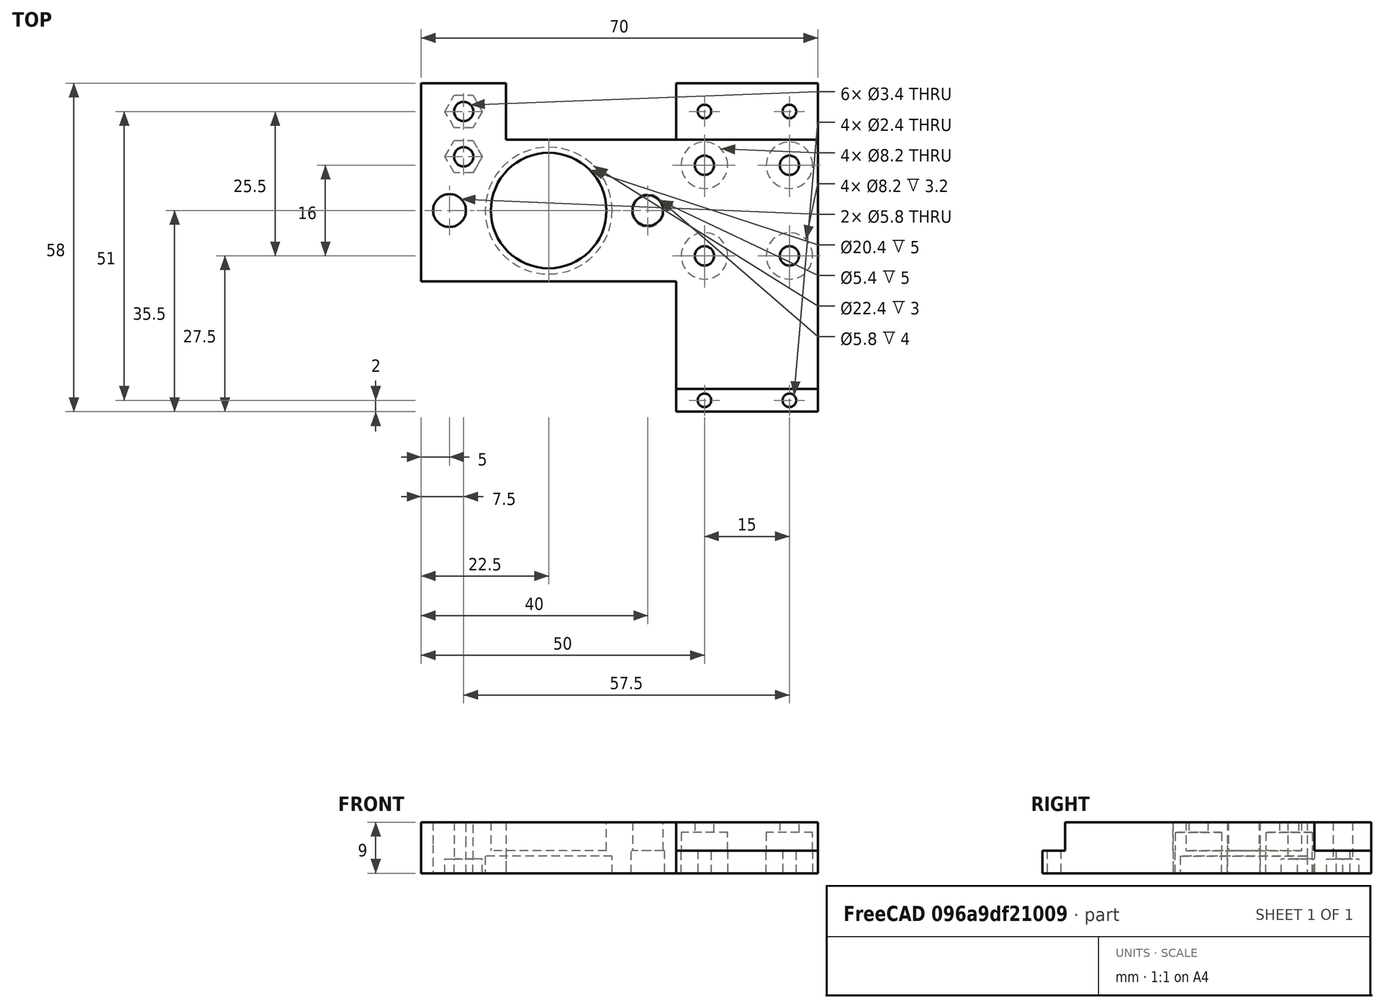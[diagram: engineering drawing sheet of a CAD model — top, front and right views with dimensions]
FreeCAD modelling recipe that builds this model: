
FCSTD DOCUMENT  (FreeCAD 0.18.4R)
Label: down_left_magnet_arm
License: All rights reserved
LicenseURL: http://en.wikipedia.org/wiki/All_rights_reserved
objects: Sketcher::SketchObject×13, PartDesign::Pocket×7, PartDesign::Pad×6, Mesh::Feature×1, PartDesign::Body×1
note: 40 computed .brp shape members not serialized (recipe doc carries the construction recipe); baked Part::Feature solids carry a one-line shape summary decoded from their .brp

FEATURE [Sketcher::SketchObject] Sketch
  MapMode = 5
  Support = -> [XY_Plane]
  sketch-geometry (10):
    g0: LineSegment StartX=-30 StartY=12.5 StartZ=0 EndX=30 EndY=12.5 EndZ=0
    g1: LineSegment StartX=30 StartY=12.5 StartZ=0 EndX=30 EndY=-12.5 EndZ=0
    g2: LineSegment StartX=30 StartY=-12.5 StartZ=0 EndX=-30 EndY=-12.5 EndZ=0
    g3: LineSegment StartX=-30 StartY=-12.5 StartZ=0 EndX=-30 EndY=12.5 EndZ=0
    g4: Circle CenterX=10 CenterY=8 CenterZ=0 NormalX=0 NormalY=0 NormalZ=1 AngleXU=0 Radius=1.7
    g5: Circle CenterX=25 CenterY=8 CenterZ=0 NormalX=0 NormalY=0 NormalZ=1 AngleXU=0 Radius=1.7
    g6: Circle CenterX=10 CenterY=-8 CenterZ=0 NormalX=0 NormalY=0 NormalZ=1 AngleXU=0 Radius=1.7
    g7: Circle CenterX=25 CenterY=-8 CenterZ=0 NormalX=0 NormalY=0 NormalZ=1 AngleXU=0 Radius=1.7
    g8: Circle CenterX=-17.5 CenterY=0 CenterZ=0 NormalX=0 NormalY=0 NormalZ=1 AngleXU=0 Radius=10.2
    g9: Circle CenterX=9e-16 CenterY=0 CenterZ=0 NormalX=0 NormalY=0 NormalZ=1 AngleXU=0 Radius=2.7
  constraints (26):
    c: Coincident(g0,g1)
    c: Coincident(g1,g2)
    c: Coincident(g2,g3)
    c: Coincident(g3,g0)
    c: Horizontal(g2)
    c: Vertical(g1)
    c: Symmetric(g0,g0,g-2)
    c: Symmetric(g0,g2,g-1)
    c: DistanceX(g0,g0) = 60
    c: DistanceY(g3,g3) = 25
    c: Symmetric(g7,g5,g-1)
    c: Symmetric(g4,g6,g-1)
    c: Distance(g6,g7) = 15
    c: Distance(g4,g6) = 16
    c: Horizontal(g5,g4)
    c: Radius(g4) = 1.7
    c: Radius(g5) = 1.7
    c: Radius(g7) = 1.7
    c: Radius(g6) = 1.7
    c: Distance(g5,g1) = 5
    c: Radius(g8) = 10.2
    c: PointOnObject(g8,g-1)
    c: Distance(g8,g3) = 12.5
    c: PointOnObject(g9,g-1)
    c: Distance(g9,g8) = 17.5
    c: Radius(g9) = 2.7
FEATURE [PartDesign::Pad] Pad
  Length = 5
  Length2 = 100
  Profile = -> Sketch
  Type = 0
FEATURE [Sketcher::SketchObject] Sketch001
  ExternalGeometry = -> [Pad]
  MapMode = 5
  Placement = pos=(0,0,0) rot=(1,0,0;3.14159rad)
  Support = -> [Pad]
  sketch-geometry (4):
    g0: Circle CenterX=25 CenterY=8 CenterZ=0 NormalX=0 NormalY=0 NormalZ=1 AngleXU=0 Radius=4.1
    g1: Circle CenterX=25 CenterY=-8 CenterZ=0 NormalX=0 NormalY=0 NormalZ=1 AngleXU=0 Radius=4.1
    g2: Circle CenterX=10 CenterY=8 CenterZ=0 NormalX=0 NormalY=0 NormalZ=1 AngleXU=0 Radius=4.1
    g3: Circle CenterX=10 CenterY=-8 CenterZ=0 NormalX=0 NormalY=0 NormalZ=1 AngleXU=0 Radius=4.1
  constraints (8):
    c: Coincident(g0,g-4)
    c: Coincident(g1,g-5)
    c: Coincident(g2,g-6)
    c: Radius(g0) = 4.1
    c: Radius(g1) = 4.1
    c: Radius(g2) = 4.1
    c: Coincident(g3,g-11)
    c: Radius(g3) = 4.1
FEATURE [PartDesign::Pocket] Pocket001
  BaseFeature = -> Pad
  Length = 3.2
  Length2 = 100
  Profile = -> Sketch001
  Type = 0
FEATURE [Sketcher::SketchObject] Sketch002
  ExternalGeometry = -> [Pocket001]
  MapMode = 5
  Placement = pos=(0,0,0) rot=(1,0,0;3.14159rad)
  Support = -> [Pocket001]
  sketch-geometry (9):
    g0: LineSegment StartX=-30 StartY=12.5 StartZ=0 EndX=30 EndY=12.5 EndZ=0
    g1: LineSegment StartX=30 StartY=12.5 StartZ=0 EndX=30 EndY=-12.5 EndZ=0
    g2: LineSegment StartX=30 StartY=-12.5 StartZ=0 EndX=-30 EndY=-12.5 EndZ=0
    g3: LineSegment StartX=-30 StartY=-12.5 StartZ=0 EndX=-30 EndY=12.5 EndZ=0
    g4: Circle CenterX=0 CenterY=0 CenterZ=0 NormalX=0 NormalY=0 NormalZ=1 AngleXU=0 Radius=2.9
    g5: Circle CenterX=10 CenterY=8 CenterZ=0 NormalX=0 NormalY=0 NormalZ=1 AngleXU=0 Radius=4.1
    g6: Circle CenterX=10 CenterY=-8 CenterZ=0 NormalX=0 NormalY=0 NormalZ=1 AngleXU=0 Radius=4.1
    g7: Circle CenterX=25 CenterY=8 CenterZ=0 NormalX=0 NormalY=0 NormalZ=1 AngleXU=0 Radius=4.1
    g8: Circle CenterX=25 CenterY=-8 CenterZ=0 NormalX=0 NormalY=0 NormalZ=1 AngleXU=0 Radius=4.1
  constraints (20):
    c: Coincident(g0,g1)
    c: Coincident(g1,g2)
    c: Coincident(g2,g3)
    c: Coincident(g3,g0)
    c: Horizontal(g0)
    c: Horizontal(g2)
    c: Vertical(g1)
    c: Vertical(g3)
    c: Coincident(g0,g-6)
    c: Coincident(g1,g-5)
    c: Coincident(g4,g-1)
    c: Coincident(g5,g-8)
    c: Coincident(g6,g-9)
    c: Coincident(g7,g-10)
    c: Coincident(g8,g-11)
    c: Radius(g4) = 2.9
    c: Radius(g5) = 4.1
    c: Radius(g7) = 4.1
    c: Radius(g8) = 4.1
    c: Radius(g6) = 4.1
FEATURE [PartDesign::Pad] Pad001
  BaseFeature = -> Pocket001
  Length = 4
  Length2 = 100
  Profile = -> Sketch002
  Type = 0
FEATURE [Sketcher::SketchObject] Sketch003
  ExternalGeometry = -> [Pad001]
  MapMode = 5
  Placement = pos=(0,0,-4) rot=(1,0,0;3.14159rad)
  Support = -> [Pad001]
  sketch-geometry (1):
    g0: Circle CenterX=-17.5 CenterY=0 CenterZ=0 NormalX=0 NormalY=0 NormalZ=1 AngleXU=0 Radius=11.2
  constraints (3):
    c: PointOnObject(g0,g-1)
    c: Radius(g0) = 11.2
    c: Distance(g0,g-4) = 12.5
FEATURE [PartDesign::Pocket] Pocket
  BaseFeature = -> Pad001
  Length = 3
  Length2 = 100
  Profile = -> Sketch003
  Type = 0
FEATURE [Sketcher::SketchObject] Sketch004
  ExternalGeometry = -> [Pocket]
  MapMode = 5
  Placement = pos=(-30,0,0) rot=(0.57735,-0.57735,-0.57735;2.0944rad)
  Support = -> [Pocket]
  sketch-geometry (4):
    g0: LineSegment StartX=12.5 StartY=-4 StartZ=0 EndX=-12.5 EndY=-4 EndZ=0
    g1: LineSegment StartX=-12.5 StartY=-4 StartZ=0 EndX=-12.5 EndY=5 EndZ=0
    g2: LineSegment StartX=-12.5 StartY=5 StartZ=0 EndX=12.5 EndY=5 EndZ=0
    g3: LineSegment StartX=12.5 StartY=5 StartZ=0 EndX=12.5 EndY=-4 EndZ=0
  constraints (12):
    c: Coincident(g0,g1)
    c: Coincident(g1,g2)
    c: Coincident(g2,g3)
    c: Coincident(g3,g0)
    c: Horizontal(g2)
    c: Vertical(g1)
    c: Vertical(g3)
    c: PointOnObject(g0,g-3)
    c: DistanceX(g0,g0) = 25
    c: Symmetric(g0,g0,g-2)
    c: PointOnObject(g1,g-4)
    c: Distance(g-3) = 25
FEATURE [PartDesign::Pad] Pad002
  BaseFeature = -> Pocket
  Length = 10
  Length2 = 100
  Profile = -> Sketch004
  Type = 0
FEATURE [Sketcher::SketchObject] Sketch005
  ExternalGeometry = -> [Pad002]
  MapMode = 5
  Placement = pos=(0,0,-4) rot=(1,0,0;3.14159rad)
  Support = -> [Pad002]
  sketch-geometry (1):
    g0: Circle CenterX=-35 CenterY=0 CenterZ=0 NormalX=0 NormalY=0 NormalZ=1 AngleXU=0 Radius=2.9
  constraints (3):
    c: PointOnObject(g0,g-1)
    c: Distance(g-3,g0) = 17.5
    c: Radius(g0) = 2.9
FEATURE [PartDesign::Pocket] Pocket002
  BaseFeature = -> Pad002
  Length = 5
  Length2 = 100
  Profile = -> Sketch005
  Type = 0
FEATURE [Mesh::Feature] belt_support_left001
  Placement = pos=(-15,-17,5) rot=(0,0,1;0rad)
FEATURE [Sketcher::SketchObject] Sketch006
  ExternalGeometry = -> [Pocket002]
  MapMode = 5
  Placement = pos=(0,-12.5,0) rot=(1,0,0;1.5708rad)
  Support = -> [Pocket002]
  sketch-geometry (4):
    g0: LineSegment StartX=30 StartY=-4 StartZ=0 EndX=5 EndY=-4 EndZ=0
    g1: LineSegment StartX=5 StartY=-4 StartZ=0 EndX=5 EndY=5 EndZ=0
    g2: LineSegment StartX=5 StartY=5 StartZ=0 EndX=30 EndY=5 EndZ=0
    g3: LineSegment StartX=30 StartY=5 StartZ=0 EndX=30 EndY=-4 EndZ=0
  constraints (11):
    c: Coincident(g0,g1)
    c: Coincident(g1,g2)
    c: Coincident(g2,g3)
    c: Coincident(g3,g0)
    c: Horizontal(g0)
    c: Horizontal(g2)
    c: Vertical(g1)
    c: Vertical(g3)
    c: Coincident(g0,g-4)
    c: Distance(g0) = 25
    c: PointOnObject(g1,g-3)
FEATURE [PartDesign::Pad] Pad003
  BaseFeature = -> Pocket002
  Length = 23
  Length2 = 100
  Profile = -> Sketch006
  Type = 0
FEATURE [Sketcher::SketchObject] Sketch007
  ExternalGeometry = -> [Pad003]
  MapMode = 5
  Placement = pos=(0,12.5,0) rot=(0,0.707107,0.707107;3.14159rad)
  Support = -> [Pad003]
  sketch-geometry (4):
    g0: LineSegment StartX=-30 StartY=-4 StartZ=0 EndX=-5 EndY=-4 EndZ=0
    g1: LineSegment StartX=-5 StartY=-4 StartZ=0 EndX=-5 EndY=0 EndZ=0
    g2: LineSegment StartX=-5 StartY=0 StartZ=0 EndX=-30 EndY=0 EndZ=0
    g3: LineSegment StartX=-30 StartY=0 StartZ=0 EndX=-30 EndY=-4 EndZ=0
  constraints (11):
    c: Coincident(g0,g1)
    c: Coincident(g1,g2)
    c: Coincident(g2,g3)
    c: Coincident(g3,g0)
    c: Horizontal(g0)
    c: Horizontal(g2)
    c: Vertical(g1)
    c: Vertical(g3)
    c: Coincident(g0,g-3)
    c: PointOnObject(g1,g-1)
    c: Distance(g0) = 25
FEATURE [PartDesign::Pad] Pad004
  BaseFeature = -> Pad003
  Length = 10
  Length2 = 100
  Profile = -> Sketch007
  Type = 0
FEATURE [Sketcher::SketchObject] Sketch008
  ExternalGeometry = -> [Pad004]
  MapMode = 5
  Placement = pos=(0,12.5,0) rot=(0,0.707107,0.707107;3.14159rad)
  Support = -> [Pad004]
  sketch-geometry (4):
    g0: LineSegment StartX=40 StartY=5 StartZ=0 EndX=25 EndY=5 EndZ=0
    g1: LineSegment StartX=25 StartY=5 StartZ=0 EndX=25 EndY=-4 EndZ=0
    g2: LineSegment StartX=25 StartY=-4 StartZ=0 EndX=40 EndY=-4 EndZ=0
    g3: LineSegment StartX=40 StartY=-4 StartZ=0 EndX=40 EndY=5 EndZ=0
  constraints (12):
    c: Coincident(g0,g1)
    c: Coincident(g1,g2)
    c: Coincident(g2,g3)
    c: Coincident(g3,g0)
    c: Horizontal(g0)
    c: Horizontal(g2)
    c: Vertical(g1)
    c: Vertical(g3)
    c: PointOnObject(g0,g-4)
    c: PointOnObject(g1,g-3)
    c: DistanceX(g2,g2) = 15
    c: PointOnObject(g0,g-5)
FEATURE [PartDesign::Pad] Pad005
  BaseFeature = -> Pad004
  Length = 10
  Length2 = 100
  Profile = -> Sketch008
  Type = 0
FEATURE [Sketcher::SketchObject] Sketch009
  ExternalGeometry = -> [Pad005]
  MapMode = 5
  Placement = pos=(0,1.1e-15,5) rot=(0,0,1;0rad)
  Support = -> [Pad005]
  sketch-geometry (4):
    g0: LineSegment StartX=5 StartY=-35.5 StartZ=0 EndX=30 EndY=-35.5 EndZ=0
    g1: LineSegment StartX=30 StartY=-35.5 StartZ=0 EndX=30 EndY=-31.5 EndZ=0
    g2: LineSegment StartX=30 StartY=-31.5 StartZ=0 EndX=5 EndY=-31.5 EndZ=0
    g3: LineSegment StartX=5 StartY=-31.5 StartZ=0 EndX=5 EndY=-35.5 EndZ=0
  constraints (11):
    c: Coincident(g0,g1)
    c: Coincident(g1,g2)
    c: Coincident(g2,g3)
    c: Coincident(g3,g0)
    c: Horizontal(g0)
    c: Horizontal(g2)
    c: Vertical(g1)
    c: Vertical(g3)
    c: Coincident(g0,g-5)
    c: PointOnObject(g1,g-4)
    c: DistanceY(g1,g1) = 4
FEATURE [PartDesign::Pocket] Pocket003
  BaseFeature = -> Pad005
  Length = 5
  Length2 = 100
  Profile = -> Sketch009
  Type = 0
FEATURE [Sketcher::SketchObject] Sketch010
  ExternalGeometry = -> [Pocket003]
  MapMode = 5
  Placement = pos=(0,-9e-16,-4) rot=(1,0,0;3.14159rad)
  Support = -> [Pocket003]
  sketch-geometry (6):
    g0: Circle CenterX=10 CenterY=33.5 CenterZ=0 NormalX=0 NormalY=0 NormalZ=1 AngleXU=0 Radius=1.2
    g1: Circle CenterX=25 CenterY=33.5 CenterZ=0 NormalX=0 NormalY=0 NormalZ=1 AngleXU=0 Radius=1.2
    g2: Circle CenterX=10 CenterY=-17.5 CenterZ=0 NormalX=0 NormalY=0 NormalZ=1 AngleXU=0 Radius=1.2
    g3: Circle CenterX=25 CenterY=-17.5 CenterZ=0 NormalX=0 NormalY=0 NormalZ=1 AngleXU=0 Radius=1.2
    g4: Circle CenterX=-32.5 CenterY=-9.5 CenterZ=0 NormalX=0 NormalY=0 NormalZ=1 AngleXU=0 Radius=1.7
    g5: Circle CenterX=-32.5 CenterY=-17.5 CenterZ=0 NormalX=0 NormalY=0 NormalZ=1 AngleXU=0 Radius=1.7
  constraints (19):
    c: Radius(g3) = 1.2
    c: Radius(g2) = 1.2
    c: Radius(g0) = 1.2
    c: Radius(g1) = 1.2
    c: Horizontal(g0,g1)
    c: Vertical(g0,g2)
    c: Horizontal(g2,g3)
    c: Vertical(g1,g3)
    c: Distance(g1,g0) = 15
    c: Distance(g2,g-5) = 5
    c: Distance(g0,g-4) = 5
    c: Distance(g0,g-3) = 2
    c: Distance(g-4) = 23
    c: Vertical(g4,g5)
    c: Distance(g4,g-6) = 7.5
    c: Radius(g4) = 1.7
    c: Radius(g5) = 1.7
    c: Distance(g5,g4) = 8
    c: Distance(g5,g-8) = 5
FEATURE [PartDesign::Pocket] Pocket004
  BaseFeature = -> Pocket003
  Length = 9
  Length2 = 100
  Profile = -> Sketch010
  Type = 0
FEATURE [Sketcher::SketchObject] Sketch011
  ExternalGeometry = -> [Pocket004]
  MapMode = 5
  Placement = pos=(0,-9e-16,-4) rot=(1,0,0;3.14159rad)
  Support = -> [Pocket004]
  sketch-geometry (14):
    g0: LineSegment StartX=-30.85 StartY=-20.3579 StartZ=0 EndX=-29.2 EndY=-17.5 EndZ=0
    g1: LineSegment StartX=-29.2 StartY=-17.5 StartZ=0 EndX=-30.85 EndY=-14.6421 EndZ=0
    g2: LineSegment StartX=-30.85 StartY=-14.6421 StartZ=0 EndX=-34.15 EndY=-14.6421 EndZ=0
    g3: LineSegment StartX=-34.15 StartY=-14.6421 StartZ=0 EndX=-35.8 EndY=-17.5 EndZ=0
    g4: LineSegment StartX=-35.8 StartY=-17.5 StartZ=0 EndX=-34.15 EndY=-20.3579 EndZ=0
    g5: LineSegment StartX=-34.15 StartY=-20.3579 StartZ=0 EndX=-30.85 EndY=-20.3579 EndZ=0
    g6: Circle [constr] CenterX=-32.5 CenterY=-17.5 CenterZ=0 NormalX=0 NormalY=0 NormalZ=1 AngleXU=0 Radius=3.3
    g7: LineSegment StartX=-34.15 StartY=-12.3579 StartZ=0 EndX=-30.85 EndY=-12.3579 EndZ=0
    g8: LineSegment StartX=-30.85 StartY=-12.3579 StartZ=0 EndX=-29.2 EndY=-9.5 EndZ=0
    g9: LineSegment StartX=-29.2 StartY=-9.5 StartZ=0 EndX=-30.85 EndY=-6.64212 EndZ=0
    g10: LineSegment StartX=-30.85 StartY=-6.64212 StartZ=0 EndX=-34.15 EndY=-6.64212 EndZ=0
    g11: LineSegment StartX=-34.15 StartY=-6.64212 StartZ=0 EndX=-35.8 EndY=-9.5 EndZ=0
    g12: LineSegment StartX=-35.8 StartY=-9.5 StartZ=0 EndX=-34.15 EndY=-12.3579 EndZ=0
    g13: Circle [constr] CenterX=-32.5 CenterY=-9.5 CenterZ=0 NormalX=0 NormalY=0 NormalZ=1 AngleXU=0 Radius=3.3
  constraints (32):
    c: Coincident(g0,g1)
    c: Coincident(g1,g2)
    c: Coincident(g2,g3)
    c: Coincident(g3,g4)
    c: Coincident(g4,g5)
    c: Coincident(g5,g0)
    c: Equal(g0, g1-g5) x5
    c: PointOnObject(g0,g6)
    c: PointOnObject(g1,g6)
    c: PointOnObject(g2,g6)
    c: PointOnObject(g3,g6)
    c: PointOnObject(g4,g6)
    c: PointOnObject(g5,g6)
    c: Coincident(g6,g-4)
    c: Radius(g6) = 3.3
    c: Coincident(g7,g8)
    c: Coincident(g8,g9)
    c: Coincident(g9,g10)
    c: Coincident(g10,g11)
    c: Coincident(g11,g12)
    c: Coincident(g12,g7)
    c: Equal(g7, g8-g12) x5
    c: PointOnObject(g7,g13)
    c: PointOnObject(g8,g13)
    c: PointOnObject(g9,g13)
    c: PointOnObject(g10,g13)
    c: PointOnObject(g11,g13)
    c: PointOnObject(g12,g13)
    c: Coincident(g13,g-3)
    c: Parallel(g7,g2)
    c: Vertical(g2,g7)
    c: Radius(g13) = 3.3
FEATURE [PartDesign::Pocket] Pocket005
  BaseFeature = -> Pocket004
  Length = 2.5
  Length2 = 100
  Profile = -> Sketch011
  Type = 0
FEATURE [Sketcher::SketchObject] Sketch012
  ExternalGeometry = -> [Pocket005]
  MapMode = 5
  Placement = pos=(0,0,1) rot=(1,0,0;3.14159rad)
  Support = -> [Pocket005]
  sketch-geometry (1):
    g0: Circle CenterX=-35 CenterY=0 CenterZ=0 NormalX=0 NormalY=0 NormalZ=1 AngleXU=0 Radius=2.9
  constraints (2):
    c: Coincident(g0,g-3)
    c: Radius(g0) = 2.9
FEATURE [PartDesign::Pocket] Pocket006
  BaseFeature = -> Pocket005
  Length = 5
  Length2 = 100
  Profile = -> Sketch012
  Type = 0
FEATURE [PartDesign::Body] Body
  Group = -> [Sketch,Pad,Sketch001,Pocket001,Sketch002,Pad001,Sketch003,Pocket,Sketch004,Pad002,Sketch005,Pocket002,Sketch006,Pad003,Sketch007,Pad004,Sketch008,Pad005,Sketch009,Pocket003,Sketch010,Pocket004,Sketch011,Pocket005,Sketch012,Pocket006]
  Origin = -> Origin
  Tip = -> Pocket006
